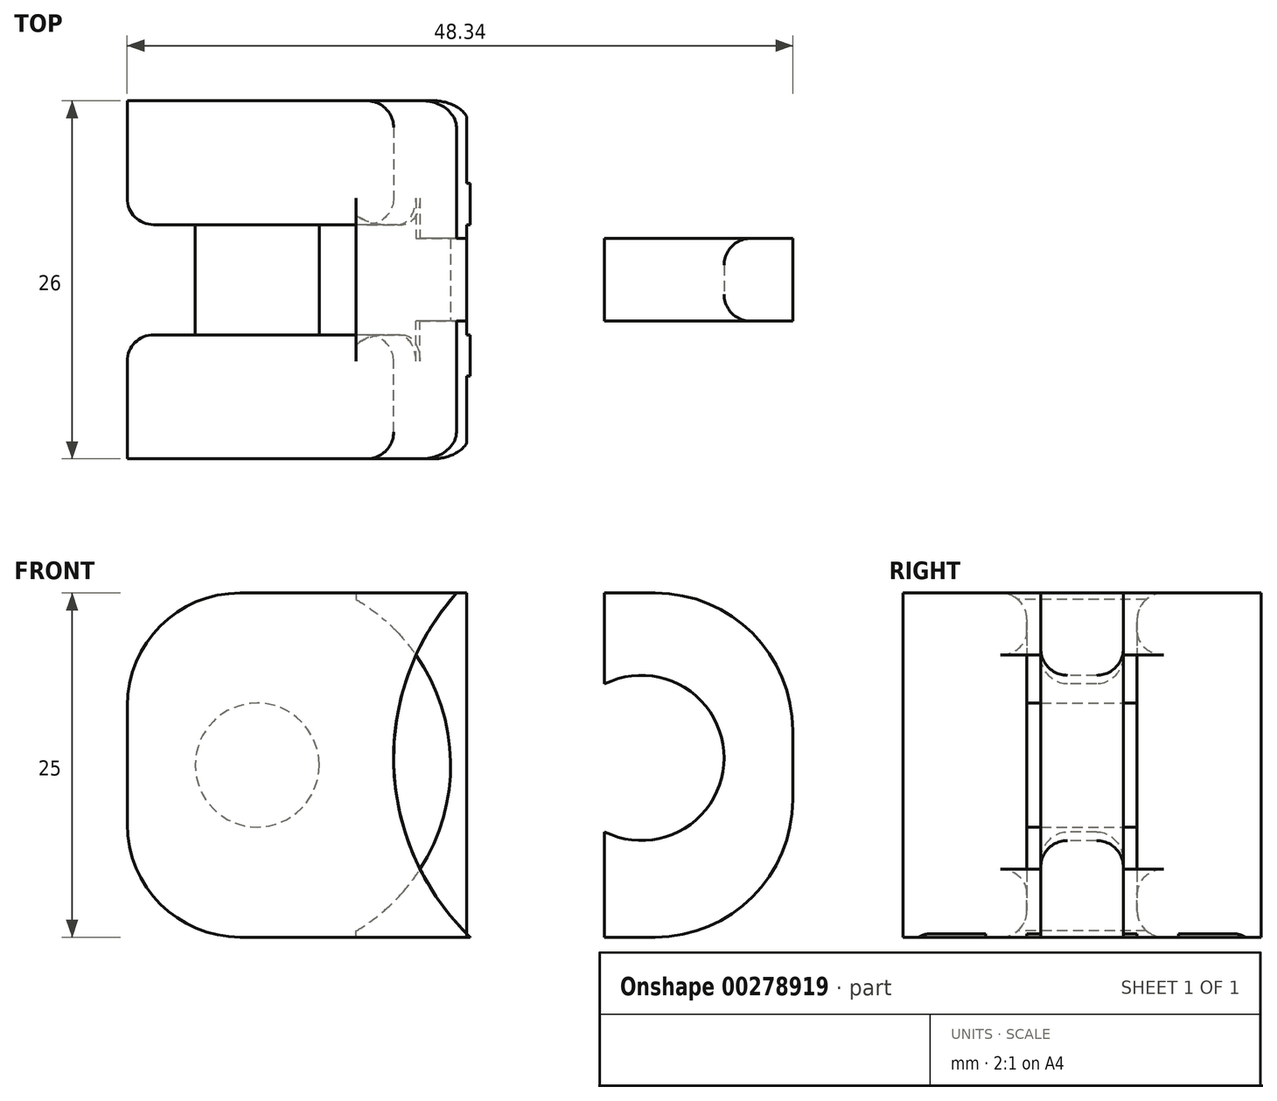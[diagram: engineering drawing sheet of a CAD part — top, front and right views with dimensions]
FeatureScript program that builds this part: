
annotation { "Feature Type Name" : "Feature", "Feature Type Description" : "" }
export const myFeature = defineFeature(function(context is Context, id is Id, definition is map)
    precondition{}
    {
        {
            var Q0;
            Q0=qCreatedBy(makeId("Top.planeOp"),FACE);
            var sketch = newSketch(context, id + "F0", { "sketchPlane" : qUnion([Q0])});
            skLineSegment(sketch, "E0.bottom", {"start": v(5, -7) * mm, "end": v(-5, -7) * mm});
            skLineSegment(sketch, "E0.top", {"start": v(5, 7) * mm, "end": v(-5, 7) * mm});
            skLineSegment(sketch, "E0.left", {"start": v(5, -7) * mm, "end": v(5, 7) * mm});
            skLineSegment(sketch, "E0.right", {"start": v(-5, -7) * mm, "end": v(-5, 7) * mm});
            skPoint(sketch, "E0.middle", {"position": v(0, 0) * mm});
            skLineSegment(sketch, "E1.bottom", {"start": v(-5, -4) * mm, "end": v(5, -4) * mm});
            skLineSegment(sketch, "E1.top", {"start": v(-5, 4) * mm, "end": v(5, 4) * mm});
            skLineSegment(sketch, "E1.left", {"start": v(-5, -4) * mm, "end": v(-5, 4) * mm});
            skLineSegment(sketch, "E1.right", {"start": v(5, -4) * mm, "end": v(5, 4) * mm});
            skLineSegment(sketch, "E2.bottom", {"start": v(0, 4) * mm, "end": v(19.67, 4) * mm});
            skLineSegment(sketch, "E2.top", {"start": v(0, -4) * mm, "end": v(19.67, -4) * mm});
            skLineSegment(sketch, "E2.left", {"start": v(0, 4) * mm, "end": v(0, -4) * mm});
            skLineSegment(sketch, "E2.right", {"start": v(19.67, 4) * mm, "end": v(19.67, -4) * mm});
            skLineSegment(sketch, "E3.0", {"start": v(0, -4.45) * mm, "end": v(12.15, -4.45) * mm});
            skLineSegment(sketch, "E4.0", {"start": v(0, -3) * mm, "end": v(18.67, -3) * mm});
            skLineSegment(sketch, "E4.1", {"start": v(18.67, 3) * mm, "end": v(18.67, -3) * mm});
            skLineSegment(sketch, "E4.2", {"start": v(0, 3) * mm, "end": v(18.67, 3) * mm});
            skLineSegment(sketch, "E5.bottom", {"start": v(-5, 13) * mm, "end": v(-29.67, 13) * mm});
            skLineSegment(sketch, "E5.top", {"start": v(-5, -13) * mm, "end": v(-29.67, -13) * mm});
            skLineSegment(sketch, "E5.left", {"start": v(-5, 13) * mm, "end": v(-5, 4) * mm});
            skLineSegment(sketch, "E5.right", {"start": v(-29.67, 13) * mm, "end": v(-29.67, -13) * mm});
            skLineSegment(sketch, "E6.MirrorCS", {"start": v(-29.67, 4) * mm, "end": v(-29.67, -4) * mm});
            skLineSegment(sketch, "E7.MirrorCS", {"start": v(-10, -4) * mm, "end": v(-29.67, -4) * mm});
            skLineSegment(sketch, "E8.MirrorCS", {"start": v(-10, 4) * mm, "end": v(-29.67, 4) * mm});
            skLineSegment(sketch, "E9.MirrorCS", {"start": v(-10, 4) * mm, "end": v(-10, -4) * mm});
            skLineSegment(sketch, "E10.trimOffspring", {"start": v(-5, -4) * mm, "end": v(-5, -13) * mm});
            skLineSegment(sketch, "E11", {"start": v(-13.04, 4) * mm, "end": v(-13.04, -4) * mm});
            skSolve(sketch);
        }
        {
            var Q0;
            {var subQ2=sQuery(id+"F0.wireOp",EDGE,"E0.top");Q0=makeQuery(id+"F0.imprint","IMPRINT",FACE,{"disambiguationData":[TD([[makeQuery(id+"F0.imprint","IMPRINT",EDGE,{"derivedFrom":subQ2}),1.0]])]});}
            var Q1;
            {var subQ2=sQuery(id+"F0.wireOp",EDGE,"E0.bottom");Q1=makeQuery(id+"F0.imprint","IMPRINT",FACE,{"disambiguationData":[TD([[makeQuery(id+"F0.imprint","IMPRINT",EDGE,{"derivedFrom":subQ2}),-1.0]])]});}
            var Q2;
            {var subQ0=sQuery(id+"F0.wireOp",EDGE,"E4.0");var subQ1=sQuery(id+"F0.wireOp",EDGE,"E1.right");var subQ2=makeQuery(id+"F0.imprint","INTERSECT",VERTEX,{"derivedFrom":[subQ1,subQ0]});Q2=makeQuery(id+"F0.imprint","IMPRINT",FACE,{"disambiguationData":[TD([[makeQuery(id+"F0.imprint","IMPRINT",EDGE,{"disambiguationData":[TD([[subQ2,-1.0]])],"derivedFrom":subQ1}),1.0]])]});}
            var Q3;
            {var subQ3=sQuery(id+"F0.wireOp",EDGE,"E4.0");var subQ5=sQuery(id+"F0.wireOp",EDGE,"E2.left");var subQ7=makeQuery(id+"F0.imprint","INTERSECT",VERTEX,{"derivedFrom":[subQ5,subQ3]});Q3=makeQuery(id+"F0.imprint","IMPRINT",FACE,{"disambiguationData":[TD([[makeQuery(id+"F0.imprint","IMPRINT",EDGE,{"disambiguationData":[TD([[subQ7,-1.0]])],"derivedFrom":subQ3}),-1.0]])]});}
            var Q4;
            {var subQ3=sQuery(id+"F0.wireOp",EDGE,"E4.2");var subQ5=sQuery(id+"F0.wireOp",EDGE,"E2.left");var subQ7=makeQuery(id+"F0.imprint","INTERSECT",VERTEX,{"derivedFrom":[subQ5,subQ3]});Q4=makeQuery(id+"F0.imprint","IMPRINT",FACE,{"disambiguationData":[TD([[makeQuery(id+"F0.imprint","IMPRINT",EDGE,{"disambiguationData":[TD([[subQ7,-1.0]])],"derivedFrom":subQ3}),1.0]])]});}
            var Q5;
            {var subQ3=sQuery(id+"F0.wireOp",EDGE,"E5.bottom");Q5=makeQuery(id+"F0.imprint","IMPRINT",FACE,{"disambiguationData":[TD([[makeQuery(id+"F0.imprint","IMPRINT",EDGE,{"derivedFrom":subQ3}),1.0]])]});}
            var Q6;
            {var subQ4=sQuery(id+"F0.wireOp",EDGE,"E1.bottom");Q6=makeQuery(id+"F0.imprint","IMPRINT",FACE,{"disambiguationData":[TD([[makeQuery(id+"F0.imprint","IMPRINT",EDGE,{"derivedFrom":subQ4}),1.0]])]});}
            var Q7;
            {var subQ5=sQuery(id+"F0.wireOp",EDGE,"E4.1");Q7=makeQuery(id+"F0.imprint","IMPRINT",FACE,{"disambiguationData":[TD([[makeQuery(id+"F0.imprint","IMPRINT",EDGE,{"derivedFrom":subQ5}),-1.0]])]});}
            var Q8;
            {var subQ0=sQuery(id+"F0.wireOp",EDGE,"E9.MirrorCS");Q8=makeQuery(id+"F0.imprint","IMPRINT",FACE,{"disambiguationData":[TD([[makeQuery(id+"F0.imprint","IMPRINT",EDGE,{"derivedFrom":subQ0}),-1.0]])]});}
            extrude(context, id + "F1", {"entities" : qUnion([Q0, Q1, Q2, Q3, Q4, Q5, Q6, Q7, Q8]), "depth" : 25 * mm});
        }
        {
            var Q0;
            Q0=makeQuery(id+"F1.opExtrude","SWEPT_FACE",FACE,{"disambiguationData":[OSD([sQuery(id+"F0.wireOp",EDGE,"E4.0")])]});
            var sketch = newSketch(context, id + "F2", { "sketchPlane" : qUnion([Q0])});
            skCircle(sketch, "E12", {"center": v(7.68, 13.02) * mm, "radius": 6 * mm});
            skSolve(sketch);
        }
        {
            var Q0;
            Q0 = qSketchRegion(id + "F2", true);
            extrude(context, id + "F3", {"entities" : qUnion([Q0]), "operationType" : NewBodyOperationType.REMOVE, "endBound" : BoundingType.SYMMETRIC, "oppositeDirection" : true, "depth" : 33.2 * mm});
        }
        {
            var Q0;
            Q0=qCreatedBy(makeId("Front.planeOp"),FACE);
            var sketch = newSketch(context, id + "F4", { "sketchPlane" : qUnion([Q0])});
            skCircle(sketch, "E13", {"center": v(-20.18, 12.5) * mm, "radius": 14 * mm});
            skSolve(sketch);
        }
        {
            var Q0;
            Q0=makeQuery(id+"F4.imprint","IMPRINT",FACE,{"disambiguationData":[TD([[makeQuery(id+"F4.imprint","IMPRINT",EDGE,{"derivedFrom":sQuery(id+"F4.wireOp",EDGE,"E13")}),1.0]])]});
            extrude(context, id + "F5", {"entities" : qUnion([Q0]), "operationType" : NewBodyOperationType.REMOVE, "endBound" : BoundingType.SYMMETRIC, "oppositeDirection" : true, "depth" : 8 * mm});
        }
        {
            var Q0;
            Q0=makeQuery(id+"F1.opExtrude","SWEPT_FACE",FACE,{"disambiguationData":[OSD([sQuery(id+"F0.wireOp",EDGE,"E5.bottom")])]});
            var sketch = newSketch(context, id + "F6", { "sketchPlane" : qUnion([Q0])});
            skCircle(sketch, "E14", {"center": v(20.23, 12.5) * mm, "radius": 4.5 * mm});
            skPoint(sketch, "E15", {"position": v(5, 12.5) * mm});
            skLineSegment(sketch, "E16", {"start": v(29.67, 12.5) * mm, "end": v(5, 12.5) * mm, "construction": true});
            skLineSegment(sketch, "E17", {"start": v(17.33, 0) * mm, "end": v(14.04, 25) * mm, "construction": true});
            skSolve(sketch);
        }
        {
            var Q0;
            Q0 = qSketchRegion(id + "F6", true);
            var Q1;
            Q1=makeQuery(id+"F1.opExtrude","SWEPT_FACE",FACE,{"disambiguationData":[OSD([sQuery(id+"F0.wireOp",EDGE,"E5.top")])]});
            extrude(context, id + "F7", {"entities" : qUnion([Q0]), "operationType" : NewBodyOperationType.ADD, "endBound" : BoundingType.UP_TO_SURFACE, "oppositeDirection" : true, "endBoundEntityFace" : qUnion([Q1]), "depth" : 25 * mm});
        }
        {
            var Q0;
            Q0=makeQuery(id+"F1.opExtrude","SWEPT_FACE",FACE,{"disambiguationData":[OSD([sQuery(id+"F0.wireOp",EDGE,"E4.0")])]});
            var sketch = newSketch(context, id + "F8", { "sketchPlane" : qUnion([Q0])});
            skCircle(sketch, "E18", {"center": v(7.68, 13.02) * mm, "radius": 18 * mm});
            skSolve(sketch);
        }
        {
            var Q0;
            Q0=makeQuery(id+"F8.imprint","IMPRINT",FACE,{"disambiguationData":[TD([[makeQuery(id+"F8.imprint","IMPRINT",EDGE,{"derivedFrom":sQuery(id+"F8.wireOp",EDGE,"E18")}),1.0]])]});
            extrude(context, id + "F9", {"entities" : qUnion([Q0]), "operationType" : NewBodyOperationType.REMOVE, "depth" : 25 * mm});
        }
        {
            var Q0;
            Q0=makeQuery(id+"F1.opExtrude","SWEPT_FACE",FACE,{"disambiguationData":[OSD([sQuery(id+"F0.wireOp",EDGE,"E4.2")])]});
            var sketch = newSketch(context, id + "F10", { "sketchPlane" : qUnion([Q0])});
            skCircle(sketch, "E19", {"center": v(-7.68, 13.02) * mm, "radius": 18 * mm});
            skSolve(sketch);
        }
        {
            var Q0;
            Q0=makeQuery(id+"F10.imprint","IMPRINT",FACE,{"disambiguationData":[TD([[makeQuery(id+"F10.imprint","IMPRINT",EDGE,{"derivedFrom":sQuery(id+"F10.wireOp",EDGE,"E19")}),1.0]])]});
            extrude(context, id + "F11", {"entities" : qUnion([Q0]), "operationType" : NewBodyOperationType.REMOVE, "depth" : 25 * mm});
        }
        {
            var Q0;
            Q0=makeQuery(id+"F1.opExtrude","CAP_EDGE",EDGE,{"disambiguationData":[OSD([sQuery(id+"F0.wireOp",EDGE,"E4.1")])],"isStart":true});
            var Q1;
            Q1=makeQuery(id+"F1.opExtrude","CAP_EDGE",EDGE,{"disambiguationData":[OSD([sQuery(id+"F0.wireOp",EDGE,"E4.1")])],"isStart":false});
            fillet(context, id + "F12", {"entities" : qUnion([Q0, Q1]), "radius" : 10 * mm, "tangentPropagation" : true, "allowEdgeOverflow" : false});
        }
        {
            var Q0;
            {var subQ0=sQuery(id+"F0.wireOp",EDGE,"E5.right");Q0=makeQuery(id+"F1.opExtrude","CAP_EDGE",EDGE,{"disambiguationData":[OSD([subQ0]),TDD([makeQuery(id+"F0.imprint","IMPRINT",EDGE,{"disambiguationData":[TD([[makeQuery(id+"F0.imprint","INTERSECT",VERTEX,{"derivedFrom":[sQuery(id+"F0.wireOp",EDGE,"E5.top"),subQ0]}),1.0]])],"derivedFrom":subQ0})])],"isStart":true});}
            var Q1;
            {var subQ0=sQuery(id+"F0.wireOp",EDGE,"E5.right");Q1=makeQuery(id+"F1.opExtrude","CAP_EDGE",EDGE,{"disambiguationData":[OSD([subQ0]),TDD([makeQuery(id+"F0.imprint","IMPRINT",EDGE,{"disambiguationData":[TD([[makeQuery(id+"F0.imprint","INTERSECT",VERTEX,{"derivedFrom":[sQuery(id+"F0.wireOp",EDGE,"E5.bottom"),subQ0]}),-1.0]])],"derivedFrom":subQ0})])],"isStart":true});}
            var Q2;
            {var subQ0=sQuery(id+"F0.wireOp",EDGE,"E5.right");Q2=makeQuery(id+"F1.opExtrude","CAP_EDGE",EDGE,{"disambiguationData":[OSD([subQ0]),TDD([makeQuery(id+"F0.imprint","IMPRINT",EDGE,{"disambiguationData":[TD([[makeQuery(id+"F0.imprint","INTERSECT",VERTEX,{"derivedFrom":[sQuery(id+"F0.wireOp",EDGE,"E5.bottom"),subQ0]}),-1.0]])],"derivedFrom":subQ0})])],"isStart":false});}
            var Q3;
            {var subQ0=sQuery(id+"F0.wireOp",EDGE,"E5.right");Q3=makeQuery(id+"F1.opExtrude","CAP_EDGE",EDGE,{"disambiguationData":[OSD([subQ0]),TDD([makeQuery(id+"F0.imprint","IMPRINT",EDGE,{"disambiguationData":[TD([[makeQuery(id+"F0.imprint","INTERSECT",VERTEX,{"derivedFrom":[sQuery(id+"F0.wireOp",EDGE,"E5.top"),subQ0]}),1.0]])],"derivedFrom":subQ0})])],"isStart":false});}
            fillet(context, id + "F13", {"entities" : qUnion([Q0, Q1, Q2, Q3]), "radius" : 8.2 * mm, "tangentPropagation" : true, "allowEdgeOverflow" : false});
        }
        {
            var Q0;
            Q0=makeQuery(id+"F3.boolean.opBoolean","INTERSECT",EDGE,{"derivedFrom":[makeQuery(id+"F1.opExtrude","SWEPT_FACE",FACE,{"disambiguationData":[OSD([sQuery(id+"F0.wireOp",EDGE,"E4.0")])]}),makeQuery(id+"F3.opExtrude","SWEPT_FACE",FACE,{"disambiguationData":[OSD([sQuery(id+"F2.wireOp",EDGE,"E12")])]})]});
            var Q1;
            Q1=makeQuery(id+"F3.boolean.opBoolean","INTERSECT",EDGE,{"derivedFrom":[makeQuery(id+"F1.opExtrude","SWEPT_FACE",FACE,{"disambiguationData":[OSD([sQuery(id+"F0.wireOp",EDGE,"E4.2")])]}),makeQuery(id+"F3.opExtrude","SWEPT_FACE",FACE,{"disambiguationData":[OSD([sQuery(id+"F2.wireOp",EDGE,"E12")])]})]});
            var Q2;
            Q2=makeQuery(id+"F11.boolean.opBoolean","INTERSECT",EDGE,{"derivedFrom":[makeQuery(id+"F5.boolean.opBoolean","MERGE",FACE,{"derivedFrom":[makeQuery(id+"F1.opExtrude","SWEPT_FACE",FACE,{"disambiguationData":[OSD([sQuery(id+"F0.wireOp",EDGE,"E8.MirrorCS")])]}),makeQuery(id+"F5.opExtrude","CAP_FACE",FACE,{"disambiguationData":[OSD([sQuery(id+"F4.wireOp",EDGE,"E13")])],"isStart":false})]}),makeQuery(id+"F11.opExtrude","SWEPT_FACE",FACE,{"disambiguationData":[OSD([sQuery(id+"F10.wireOp",EDGE,"E19")])]})]});
            var Q3;
            Q3=makeQuery(id+"F9.boolean.opBoolean","INTERSECT",EDGE,{"derivedFrom":[makeQuery(id+"F5.boolean.opBoolean","MERGE",FACE,{"derivedFrom":[makeQuery(id+"F1.opExtrude","SWEPT_FACE",FACE,{"disambiguationData":[OSD([sQuery(id+"F0.wireOp",EDGE,"E7.MirrorCS")])]}),makeQuery(id+"F5.opExtrude","CAP_FACE",FACE,{"disambiguationData":[OSD([sQuery(id+"F4.wireOp",EDGE,"E13")])],"isStart":true})]}),makeQuery(id+"F9.opExtrude","SWEPT_FACE",FACE,{"disambiguationData":[OSD([sQuery(id+"F8.wireOp",EDGE,"E18")])]})]});
            var Q4;
            {var subQ0=sQuery(id+"F0.wireOp",EDGE,"E8.MirrorCS");var subQ1=sQuery(id+"F0.wireOp",EDGE,"E5.right");Q4=makeQuery(id+"F13.opFillet","BLEND_EDGE",EDGE,{"blendedFrom":[makeQuery(id+"F1.opExtrude","CAP_EDGE",EDGE,{"disambiguationData":[OSD([subQ1]),TDD([makeQuery(id+"F0.imprint","IMPRINT",EDGE,{"disambiguationData":[TD([[makeQuery(id+"F0.imprint","INTERSECT",VERTEX,{"derivedFrom":[sQuery(id+"F0.wireOp",EDGE,"E5.bottom"),subQ1]}),-1.0]])],"derivedFrom":subQ1})])],"isStart":true}),makeQuery(id+"F5.boolean.opBoolean","MERGE",FACE,{"derivedFrom":[makeQuery(id+"F1.opExtrude","SWEPT_FACE",FACE,{"disambiguationData":[OSD([subQ0])]}),makeQuery(id+"F5.opExtrude","CAP_FACE",FACE,{"disambiguationData":[OSD([sQuery(id+"F4.wireOp",EDGE,"E13")])],"isStart":false})]})],"blendedInto":[makeQuery(id+"F5.boolean.opBoolean","MERGE",FACE,{"derivedFrom":[makeQuery(id+"F1.opExtrude","SWEPT_FACE",FACE,{"disambiguationData":[OSD([subQ0])]}),makeQuery(id+"F5.opExtrude","CAP_FACE",FACE,{"disambiguationData":[OSD([sQuery(id+"F4.wireOp",EDGE,"E13")])],"isStart":false})]})]});}
            var Q5;
            {var subQ0=sQuery(id+"F0.wireOp",EDGE,"E7.MirrorCS");var subQ1=sQuery(id+"F0.wireOp",EDGE,"E5.right");Q5=makeQuery(id+"F13.opFillet","BLEND_EDGE",EDGE,{"blendedFrom":[makeQuery(id+"F1.opExtrude","CAP_EDGE",EDGE,{"disambiguationData":[OSD([subQ1]),TDD([makeQuery(id+"F0.imprint","IMPRINT",EDGE,{"disambiguationData":[TD([[makeQuery(id+"F0.imprint","INTERSECT",VERTEX,{"derivedFrom":[sQuery(id+"F0.wireOp",EDGE,"E5.top"),subQ1]}),1.0]])],"derivedFrom":subQ1})])],"isStart":true}),makeQuery(id+"F5.boolean.opBoolean","MERGE",FACE,{"derivedFrom":[makeQuery(id+"F1.opExtrude","SWEPT_FACE",FACE,{"disambiguationData":[OSD([subQ0])]}),makeQuery(id+"F5.opExtrude","CAP_FACE",FACE,{"disambiguationData":[OSD([sQuery(id+"F4.wireOp",EDGE,"E13")])],"isStart":true})]})],"blendedInto":[makeQuery(id+"F5.boolean.opBoolean","MERGE",FACE,{"derivedFrom":[makeQuery(id+"F1.opExtrude","SWEPT_FACE",FACE,{"disambiguationData":[OSD([subQ0])]}),makeQuery(id+"F5.opExtrude","CAP_FACE",FACE,{"disambiguationData":[OSD([sQuery(id+"F4.wireOp",EDGE,"E13")])],"isStart":true})]})]});}
            var Q6;
            Q6=makeQuery(id+"F9.boolean.opBoolean","INTERSECT",EDGE,{"derivedFrom":[makeQuery(id+"F1.opExtrude","SWEPT_FACE",FACE,{"disambiguationData":[OSD([sQuery(id+"F0.wireOp",EDGE,"E5.top")])]}),makeQuery(id+"F9.opExtrude","SWEPT_FACE",FACE,{"disambiguationData":[OSD([sQuery(id+"F8.wireOp",EDGE,"E18")])]})]});
            var Q7;
            Q7=makeQuery(id+"F11.boolean.opBoolean","INTERSECT",EDGE,{"derivedFrom":[makeQuery(id+"F1.opExtrude","SWEPT_FACE",FACE,{"disambiguationData":[OSD([sQuery(id+"F0.wireOp",EDGE,"E5.bottom")])]}),makeQuery(id+"F11.opExtrude","SWEPT_FACE",FACE,{"disambiguationData":[OSD([sQuery(id+"F10.wireOp",EDGE,"E19")])]})]});
            fillet(context, id + "F14", {"entities" : qUnion([Q0, Q1, Q2, Q3, Q4, Q5, Q6, Q7]), "radius" : 1.93 * mm, "tangentPropagation" : true, "allowEdgeOverflow" : false});
        }
    });
